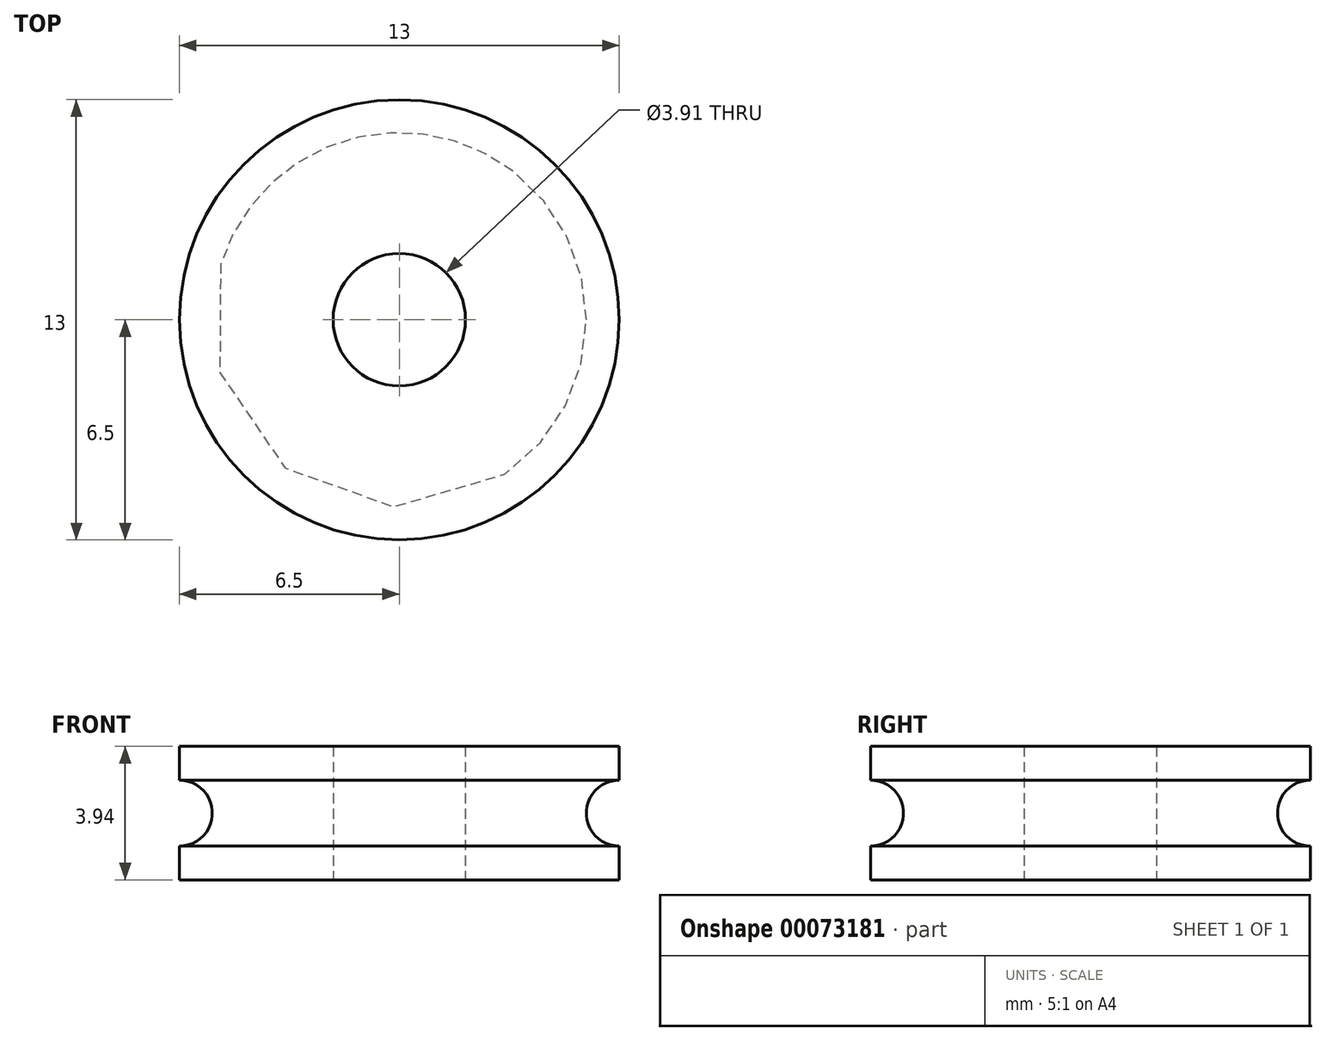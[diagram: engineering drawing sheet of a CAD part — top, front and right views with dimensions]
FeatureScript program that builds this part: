
annotation { "Feature Type Name" : "Feature", "Feature Type Description" : "" }
export const myFeature = defineFeature(function(context is Context, id is Id, definition is map)
    precondition{}
    {
        {
            var Q0;
            Q0=qCreatedBy(makeId("Top.planeOp"),FACE);
            var sketch = newSketch(context, id + "F0", { "sketchPlane" : qUnion([Q0])});
            skCircle(sketch, "E0", {"center": v(0, 0) * mm, "radius": 6.5 * mm});
            skCircle(sketch, "E1", {"center": v(0, 0) * mm, "radius": 1.96 * mm});
            skSolve(sketch);
        }
        {
            var Q0;
            Q0 = qSketchRegion(id + "F0", true);
            extrude(context, id + "F1", {"entities" : qUnion([Q0]), "depth" : 3.94 * mm});
        }
        {
            var Q0;
            Q0=qCreatedBy(makeId("Right.planeOp"),FACE);
            var sketch = newSketch(context, id + "F2", { "sketchPlane" : qUnion([Q0])});
            skCircle(sketch, "E2", {"center": v(-6.5, 1.97) * mm, "radius": 0.97 * mm});
            skLineSegment(sketch, "E3", {"start": v(0, 0) * mm, "end": v(0, 7.4) * mm, "construction": true});
            skSolve(sketch);
        }
        {
            var Q0;
            Q0 = qSketchRegion(id + "F2", true);
            var Q1;
            Q1=sQuery(id+"F2.wireOp",EDGE,"E3");
            revolve(context, id + "F3", {"operationType" : NewBodyOperationType.REMOVE, "entities" : qUnion([Q0]), "axis" : qUnion([Q1]), "revolveType" : RevolveType.FULL, "oppositeDirection" : true});
        }
    });
